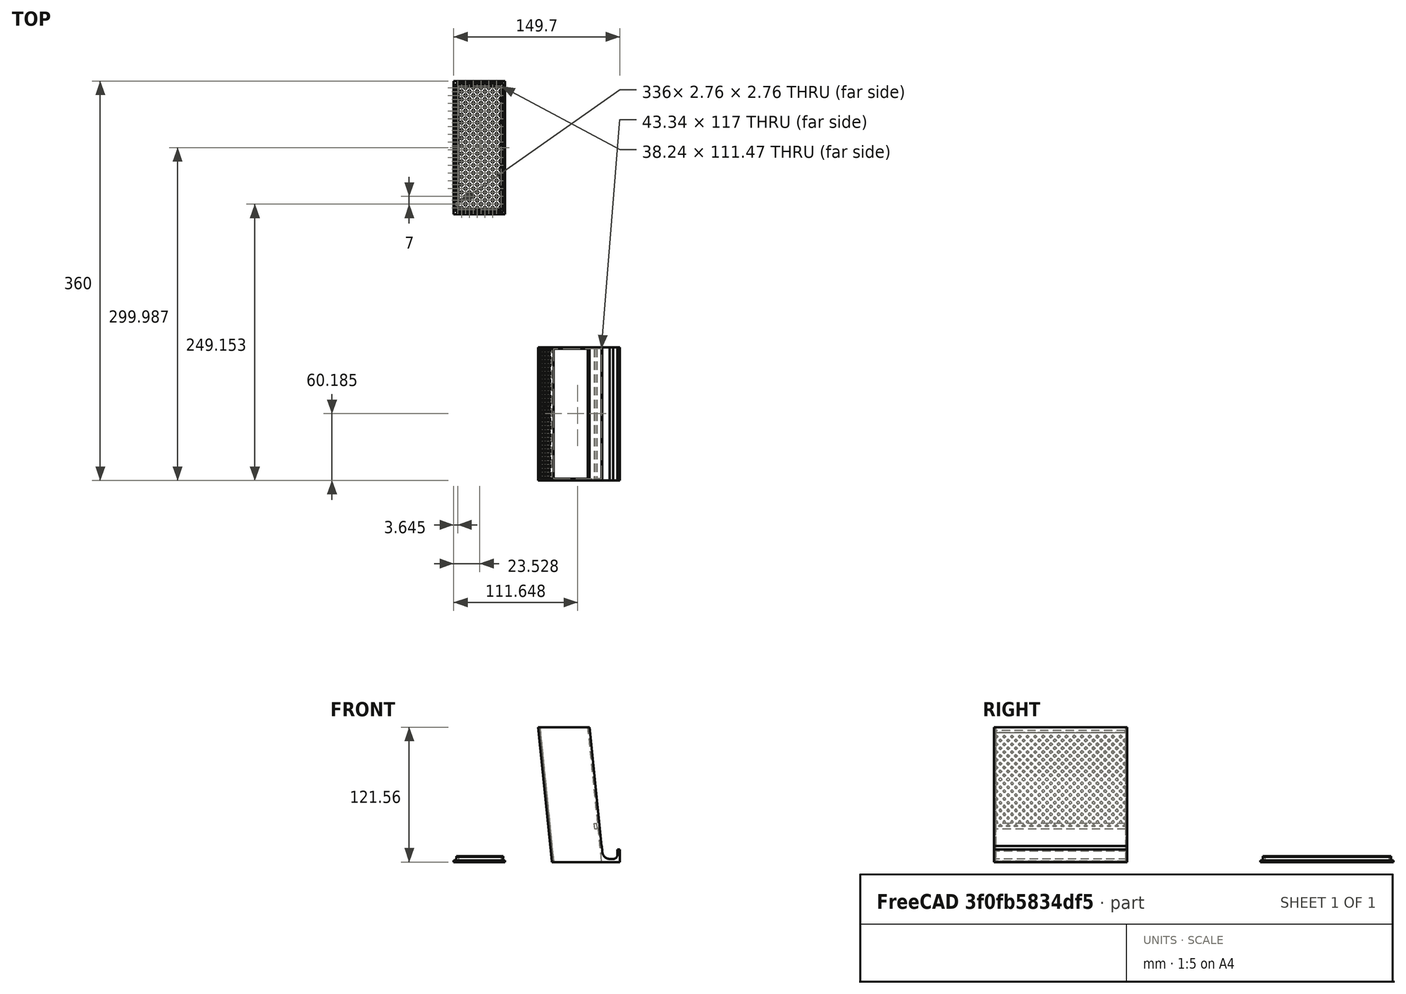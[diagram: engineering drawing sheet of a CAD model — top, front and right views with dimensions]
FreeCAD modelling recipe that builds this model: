
FCSTD DOCUMENT  (FreeCAD 0.18.4R)
Label: container.v2
License: All rights reserved
LicenseURL: http://en.wikipedia.org/wiki/All_rights_reserved
objects: Part::Extrusion×11, Part::Feature×9, Part::Part2DObjectPython×9, Part::MultiFuse×8, Part::Cut×3, Part::FeaturePython×2, Part::MultiCommon×1, App::DocumentObjectGroup×1
note: 43 computed .brp shape members not serialized (recipe doc carries the construction recipe); baked Part::Feature solids carry a one-line shape summary decoded from their .brp

FEATURE [Part::Feature] Fusion018002001008002  label="Fusion018002001010"
  shape: bbox 73.48 x 120 x 121.6 mm, 1765 faces (baked)
FEATURE [Part::Part2DObjectPython] Rectangle008  # Draft 2D object (typed FeaturePython)
  ChamferSize = 0
  Columns = 1
  FilletRadius = 0
  Height = 2.0664
  Length = 46.2967
  MakeFace = true
  Placement = pos=(-10.559,127.223,-9.82831) rot=(1,0,0;1.5708rad)
  Rows = 1
FEATURE [Part::Feature] Slice_child  label="Slice.009"
  Placement = pos=(-25.4634,240,68.2864) rot=(0,1,0;1.67207rad)
  shape: bbox 122.3 x 120 x 1.591 mm, 1756 faces (baked)
FEATURE [Part::Extrusion] Extrusion008
  Base = -> Rectangle008
  Dir = (1.277e-13,120,-2.66e-14)
  DirMode = 0
  FaceMakerClass = Part::FaceMakerBullseye
  LengthFwd = 0
  LengthRev = 0
  Solid = true
  Symmetric = false
FEATURE [Part::MultiCommon] Common
  Shapes = -> [Slice_child,Extrusion008]
FEATURE [Part::Part2DObjectPython] Rectangle009  # Draft 2D object (typed FeaturePython)
  ChamferSize = 0
  Columns = 1
  FilletRadius = 0
  Height = 1.49231
  Length = 120
  MakeFace = true
  Placement = pos=(35.7377,127.223,-9.82831) rot=(0.57735,0.57735,0.57735;2.0944rad)
  Rows = 1
  Support = -> [Common]
FEATURE [Part::Extrusion] Extrusion009
  Base = -> Rectangle009
  Dir = (-2,0,0)
  DirMode = 0
  FaceMakerClass = Part::FaceMakerBullseye
  LengthFwd = 0
  LengthRev = 0
  Solid = true
  Symmetric = false
FEATURE [Part::MultiFuse] Fusion018002001008003
  Shapes = -> [Extrusion009,Common]
FEATURE [Part::Part2DObjectPython] Rectangle010  # Draft 2D object (typed FeaturePython)
  ChamferSize = 0
  Columns = 1
  FilletRadius = 0
  Height = 1.49231
  Length = 120
  MakeFace = true
  Placement = pos=(-10.559,247.223,-9.82831) rot=(0.57735,-0.57735,-0.57735;2.0944rad)
  Rows = 1
  Support = -> [Fusion018002001008003]
FEATURE [Part::Extrusion] Extrusion010
  Base = -> Rectangle010
  Dir = (2,4.3168e-12,-6.99e-14)
  DirMode = 0
  FaceMakerClass = Part::FaceMakerBullseye
  LengthFwd = 0
  LengthRev = 0
  Solid = true
  Symmetric = false
FEATURE [Part::Feature] Face002
  shape: bbox 42.3 x 9.796e-07 x 1.492 mm, 1 faces, 0 solids (baked)
FEATURE [Part::Feature] Face004
  shape: bbox 42.3 x 9.796e-07 x 1.492 mm, 1 faces, 0 solids (baked)
FEATURE [Part::MultiFuse] Fusion018002001008004
  Shapes = -> [Extrusion010,Fusion018002001008003]
FEATURE [Part::Extrusion] Extrusion015
  Base = -> Face002
  Dir = (-1.6e-15,-2.2811,1.7e-15)
  DirMode = 0
  FaceMakerClass = Part::FaceMakerBullseye
  LengthFwd = 0
  LengthRev = 0
  Solid = true
  Symmetric = false
FEATURE [Part::Extrusion] Extrusion016
  Base = -> Face004
  Dir = (2.3e-15,2.25,-3e-16)
  DirMode = 0
  FaceMakerClass = Part::FaceMakerBullseye
  LengthFwd = 0
  LengthRev = 0
  Solid = true
  Symmetric = false
FEATURE [Part::MultiFuse] Fusion018002001008005
  Shapes = -> [Extrusion015,Fusion018002001008004]
FEATURE [Part::MultiFuse] Fusion018002001008006
  Shapes = -> [Extrusion016,Fusion018002001008005]
FEATURE [Part::Feature] Extrusion014
  Placement = pos=(-171.25,8.22981,-1.28527) rot=(0,0,1;0rad)
  shape: bbox 42.79 x 115.5 x 5.126 mm, 6 faces (baked)
FEATURE [Part::MultiFuse] Fusion018002001008007
  Shapes = -> [Fusion018002001008006,Extrusion014]
FEATURE [Part::Part2DObjectPython] Rectangle013  # Draft 2D object (typed FeaturePython)
  ChamferSize = 0
  Columns = 1
  FilletRadius = 0
  Height = 163.185
  Length = 98.735
  MakeFace = true
  Placement = pos=(-57.4113,244.942,-4.67744) rot=(1,0,0;3.14159rad)
  Rows = 1
  Support = -> [Fusion018002001008007]
FEATURE [Part::Extrusion] Extrusion017
  Base = -> Rectangle013
  Dir = (-3e-16,2e-16,2)
  DirMode = 0
  FaceMakerClass = Part::FaceMakerBullseye
  LengthFwd = 0
  LengthRev = 0
  Solid = true
  Symmetric = false
FEATURE [Part::Part2DObjectPython] Rectangle014  # Draft 2D object (typed FeaturePython)
  ChamferSize = 0
  Columns = 1
  FilletRadius = 0
  Height = 111.469
  Length = 38.2444
  MakeFace = true
  Placement = pos=(32.09,242.942,-4.67744) rot=(0,0,1;3.14159rad)
  Rows = 1
FEATURE [Part::Cut] Cut008014
  Base = -> Fusion018002001008007
  Tool = -> Extrusion017
FEATURE [Part::Extrusion] Extrusion018
  Base = -> Rectangle014
  Dir = (5e-16,-4e-16,-3.65856)
  DirMode = 0
  FaceMakerClass = Part::FaceMakerBullseye
  LengthFwd = 0
  LengthRev = 0
  Solid = true
  Symmetric = false
FEATURE [Part::Cut] Cut008015
  Base = -> Cut008014
  Tool = -> Extrusion018
FEATURE [Part::Feature] Cut008015_solid  label="Cut008015 (Solid)"
  shape: bbox 46.3 x 120 x 5.151 mm, 1088 faces (baked)
FEATURE [Part::Feature] Face005
  shape: bbox 1.805 x 8.269e-07 x 3 mm, 1 faces, 0 solids (baked)
FEATURE [Part::Extrusion] Extrusion
  Base = -> Face005
  Dir = (1.735e-13,-118,-1.18e-14)
  DirMode = 0
  FaceMakerClass = Part::FaceMakerBullseye
  LengthFwd = 0
  LengthRev = 0
  Solid = true
  Symmetric = false
FEATURE [Part::Part2DObjectPython] Rectangle  label="Rectangle016"  # Draft 2D object (typed FeaturePython)
  ChamferSize = 0
  Columns = 1
  FilletRadius = 0
  Height = 159.931
  Length = 104.027
  MakeFace = true
  Placement = pos=(-39.4242,127.223,-5.336) rot=(0,0,1;0rad)
  Rows = 1
FEATURE [Part::FeaturePython] Slice  # WARN: FeaturePython — macro-defined, semantics opaque (R4)
  Base = -> Cut008015
  Mode = 1
  Tolerance = 0
  Tools = -> [Rectangle]
FEATURE [Part::FeaturePython] Slice_child0  label="Slice.0"  # WARN: FeaturePython — macro-defined, semantics opaque (R4)
  Base = -> Slice
  FilterType = 1
  Invert = false
  OverrideMaxVal = 0
  WindowFrom = 80
  WindowTo = 100
  items = 0
FEATURE [App::DocumentObjectGroup] GrExplode_Slice  label="Exploded Slice"
  Group = -> [Slice_child0]
FEATURE [Part::MultiFuse] Fusion
  Shapes = -> [Fusion018002001008002,Extrusion]
FEATURE [Part::Part2DObjectPython] Rectangle022  label="Rectangle023"  # Draft 2D object (typed FeaturePython)
  ChamferSize = 0
  Columns = 1
  FilletRadius = 0
  Height = 1.98975
  Length = 6.79779
  MakeFace = true
  Placement = pos=(62.5688,5.2227,108.726) rot=(-1,0,0;1.5708rad)
  Rows = 1
FEATURE [Part::Extrusion] Extrusion019
  Base = -> Rectangle022
  Dir = (-8.24e-14,-116,7.73e-14)
  DirMode = 0
  FaceMakerClass = Part::FaceMakerBullseye
  LengthFwd = 0
  LengthRev = 0
  Solid = true
  Symmetric = false
FEATURE [Part::Cut] Cut
  Base = -> Fusion
  Tool = -> Extrusion019
FEATURE [Part::Part2DObjectPython] Wire  # Draft 2D object (typed FeaturePython)
  ChamferSize = 0
  Closed = true
  End = (118.208,7.2227,24.991)
  FilletRadius = 0
  Length = 14
  MakeFace = true
  Placement = pos=(118.715,7.2227,20.0168) rot=(-1,0,0;1.5708rad)
  Points = (4) [(0,0,0),(-2,0,-1.77636e-15),(-2.50744,-4.97418,-6.21725e-15),(-0.507443,-4.97418,6.92779e-14)]
  Start = (118.715,7.2227,20.0168)
  Subdivisions = 0
FEATURE [Part::Extrusion] Extrusion020
  Base = -> Wire
  Dir = (2.2329e-12,-120,1.0985e-12)
  DirMode = 0
  FaceMakerClass = Part::FaceMakerBullseye
  LengthFwd = 0
  LengthRev = 0
  Solid = true
  Symmetric = false
FEATURE [Part::MultiFuse] Fusion018002001008008
  Shapes = -> [Cut,Extrusion020]
FEATURE [Part::Part2DObjectPython] Wire001  # Draft 2D object (typed FeaturePython)
  ChamferSize = 0
  Closed = true
  End = (66.3257,7.2227,105.202)
  FilletRadius = 0
  Length = 5.92352
  MakeFace = true
  Placement = pos=(67.8104,7.2227,105.353) rot=(-1,0,0;1.5708rad)
  Points = (4) [(0,0,0),(-0.140513,-1.38265,3.55271e-14),(-1.64051,-1.38265,3.4639e-14),(-1.48467,0.150881,4.44089e-15)]
  Start = (67.8104,7.2227,105.353)
  Subdivisions = 0
FEATURE [Part::Extrusion] Extrusion021
  Base = -> Wire001
  Dir = (-2.945e-13,-120,2.814e-12)
  DirMode = 0
  FaceMakerClass = Part::FaceMakerBullseye
  LengthFwd = 0
  LengthRev = 0
  Solid = true
  Symmetric = false
FEATURE [Part::MultiFuse] Fusion018002001008009
  Shapes = -> [Fusion018002001008008,Extrusion021]
FEATURE [Part::Feature] Fusion018002001008009001  label="Fusion018002001008010"
  shape: bbox 73.48 x 120 x 121.6 mm, 1698 faces (baked)
FEATURE [Part::Feature] Slice_child0001  label="Slice.010"
  shape: bbox 46.3 x 120 x 4.492 mm, 899 faces (baked)
